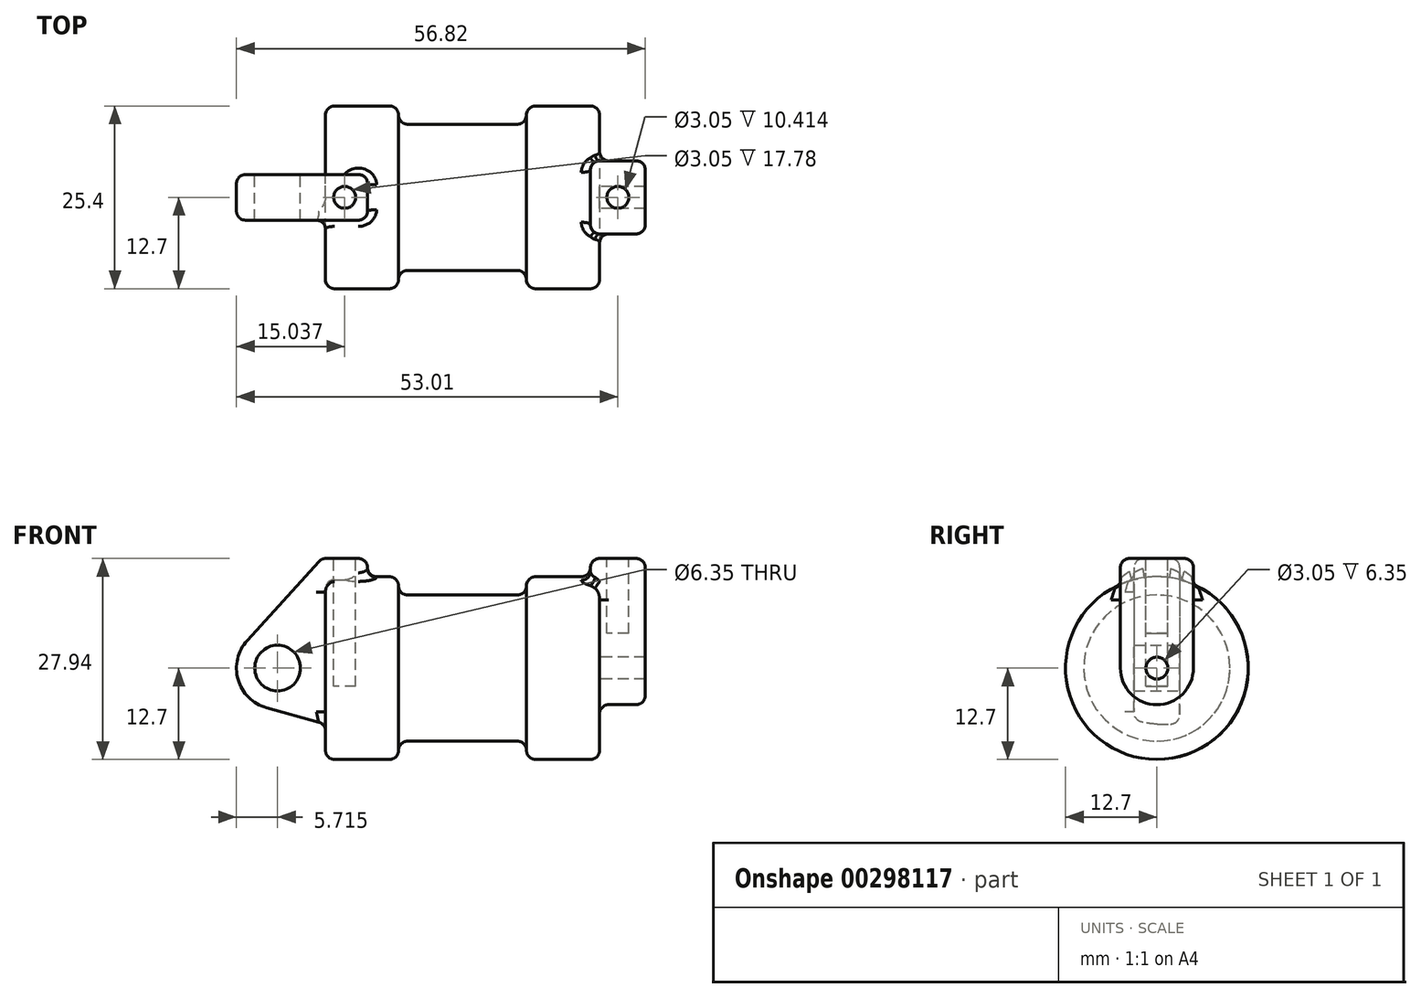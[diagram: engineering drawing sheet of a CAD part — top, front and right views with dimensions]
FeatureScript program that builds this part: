
annotation { "Feature Type Name" : "Feature", "Feature Type Description" : "" }
export const myFeature = defineFeature(function(context is Context, id is Id, definition is map)
    precondition{}
    {
        {
            var Q0;
            Q0=qCreatedBy(makeId("Front.planeOp"),FACE);
            var sketch = newSketch(context, id + "F0", { "sketchPlane" : qUnion([Q0])});
            skLineSegment(sketch, "E0", {"start": v(0, 0) * mm, "end": v(0, 12.7) * mm});
            skLineSegment(sketch, "E1", {"start": v(0, 12.7) * mm, "end": v(10.16, 12.7) * mm});
            skLineSegment(sketch, "E2", {"start": v(10.16, 12.7) * mm, "end": v(10.16, 10.16) * mm});
            skLineSegment(sketch, "E3", {"start": v(10.16, 10.16) * mm, "end": v(27.94, 10.16) * mm});
            skLineSegment(sketch, "E4", {"start": v(27.94, 10.16) * mm, "end": v(27.94, 12.7) * mm});
            skLineSegment(sketch, "E5", {"start": v(27.94, 12.7) * mm, "end": v(38.1, 12.7) * mm});
            skLineSegment(sketch, "E6", {"start": v(38.1, 12.7) * mm, "end": v(38.1, 0) * mm});
            skLineSegment(sketch, "E7", {"start": v(38.1, 0) * mm, "end": v(0, 0) * mm});
            skLineSegment(sketch, "E8", {"start": v(5.84, 15.24) * mm, "end": v(-0.5, 15.24) * mm});
            skLineSegment(sketch, "E9", {"start": v(-0.5, 15.24) * mm, "end": v(-10.88, 3.85) * mm});
            skLineSegment(sketch, "E10", {"start": v(0, 0) * mm, "end": v(-6.65, 0) * mm});
            skCircle(sketch, "E11", {"center": v(-6.65, 0) * mm, "radius": 5.72 * mm});
            skCircle(sketch, "E12", {"center": v(-6.65, 0) * mm, "radius": 3.18 * mm});
            skLineSegment(sketch, "E13", {"start": v(5.84, 15.24) * mm, "end": v(5.84, -9.4) * mm});
            skLineSegment(sketch, "E14", {"start": v(5.84, -9.4) * mm, "end": v(-8.18, -5.5) * mm});
            skSolve(sketch);
        }
        {
            var Q0;
            {var subQ0=sQuery(id+"F0.wireOp",EDGE,"E2");Q0=makeQuery(id+"F0.imprint","IMPRINT",FACE,{"disambiguationData":[TD([[makeQuery(id+"F0.imprint","IMPRINT",EDGE,{"derivedFrom":subQ0}),-1.0]])]});}
            var Q1;
            {var subQ0=sQuery(id+"F0.wireOp",EDGE,"E0");Q1=makeQuery(id+"F0.imprint","IMPRINT",FACE,{"disambiguationData":[TD([[makeQuery(id+"F0.imprint","IMPRINT",EDGE,{"derivedFrom":subQ0}),-1.0]])]});}
            var Q2;
            Q2=sQuery(id+"F0.wireOp",EDGE,"E7");
            revolve(context, id + "F1", {"entities" : qUnion([Q0, Q1]), "axis" : qUnion([Q2]), "revolveType" : RevolveType.FULL});
        }
        {
            var Q0;
            {var subQ1=sQuery(id+"F0.wireOp",EDGE,"E0");Q0=makeQuery(id+"F0.imprint","IMPRINT",FACE,{"disambiguationData":[TD([[makeQuery(id+"F0.imprint","IMPRINT",EDGE,{"derivedFrom":subQ1}),1.0]])]});}
            var Q1;
            Q1=makeQuery(id+"F0.imprint","IMPRINT",FACE,{"disambiguationData":[TD([[makeQuery(id+"F0.imprint","IMPRINT",EDGE,{"derivedFrom":sQuery(id+"F0.wireOp",EDGE,"E12")}),-1.0]])]});
            var Q2;
            {var subQ0=sQuery(id+"F0.wireOp",EDGE,"E14");Q2=makeQuery(id+"F0.imprint","IMPRINT",FACE,{"disambiguationData":[TD([[makeQuery(id+"F0.imprint","IMPRINT",EDGE,{"derivedFrom":subQ0}),-1.0]])]});}
            var Q3;
            {var subQ0=sQuery(id+"F0.wireOp",EDGE,"E0");Q3=makeQuery(id+"F0.imprint","IMPRINT",FACE,{"disambiguationData":[TD([[makeQuery(id+"F0.imprint","IMPRINT",EDGE,{"derivedFrom":subQ0}),-1.0]])]});}
            extrude(context, id + "F2", {"entities" : qUnion([Q0, Q1, Q2, Q3]), "operationType" : NewBodyOperationType.ADD, "endBound" : BoundingType.SYMMETRIC, "depth" : 6.35 * mm});
        }
        {
            var Q0;
            Q0=makeQuery(id+"F1.opRevolve","SWEPT_FACE",FACE,{"disambiguationData":[OSD([sQuery(id+"F0.wireOp",EDGE,"E6")])]});
            var sketch = newSketch(context, id + "F3", { "sketchPlane" : qUnion([Q0])});
            skCircle(sketch, "E15", {"center": v(0, 0) * mm, "radius": 5.08 * mm});
            skCircle(sketch, "E16", {"center": v(0, 0) * mm, "radius": 1.52 * mm});
            skLineSegment(sketch, "E17", {"start": v(-5.08, 0) * mm, "end": v(-5.08, 15.24) * mm});
            skLineSegment(sketch, "E18", {"start": v(5.08, 0) * mm, "end": v(5.08, 15.24) * mm});
            skLineSegment(sketch, "E19", {"start": v(5.08, 15.24) * mm, "end": v(-5.08, 15.24) * mm});
            skSolve(sketch);
        }
        {
            var Q0;
            {var subQ0=sQuery(id+"F3.wireOp",EDGE,"E19");Q0=makeQuery(id+"F3.imprint","IMPRINT",FACE,{"disambiguationData":[TD([[makeQuery(id+"F3.imprint","IMPRINT",EDGE,{"derivedFrom":subQ0}),1.0]])]});}
            var Q1;
            {var subQ0=sQuery(id+"F3.wireOp",EDGE,"E17");var subQ1=sQuery(id+"F3.wireOp",EDGE,"E15");var subQ2=makeQuery(id+"F3.imprint","INTERSECT",VERTEX,{"derivedFrom":[subQ1,subQ0]});Q1=makeQuery(id+"F3.imprint","IMPRINT",FACE,{"disambiguationData":[TD([[makeQuery(id+"F3.imprint","IMPRINT",EDGE,{"disambiguationData":[TD([[subQ2,1.0]])],"derivedFrom":subQ1}),-1.0]])]});}
            var Q2;
            Q2=makeQuery(id+"F3.imprint","IMPRINT",FACE,{"disambiguationData":[TD([[makeQuery(id+"F3.imprint","IMPRINT",EDGE,{"derivedFrom":sQuery(id+"F3.wireOp",EDGE,"E16")}),-1.0]])]});
            extrude(context, id + "F4", {"entities" : qUnion([Q0, Q1, Q2]), "operationType" : NewBodyOperationType.ADD, "depth" : 6.35 * mm, "hasSecondDirection" : true, "secondDirectionOppositeDirection" : true, "secondDirectionDepth" : 1.27 * mm});
        }
        {
            var Q0;
            Q0=makeQuery(id+"F4.opExtrude","SWEPT_FACE",FACE,{"disambiguationData":[OSD([sQuery(id+"F3.wireOp",EDGE,"E19")])]});
            var sketch = newSketch(context, id + "F5", { "sketchPlane" : qUnion([Q0])});
            skLineSegment(sketch, "E20", {"start": v(40.64, 5.08) * mm, "end": v(40.64, -5.08) * mm, "construction": true});
            skLineSegment(sketch, "E21", {"start": v(44.45, 0) * mm, "end": v(36.83, 0) * mm, "construction": true});
            skCircle(sketch, "E22", {"center": v(40.64, 0) * mm, "radius": 1.52 * mm});
            skSolve(sketch);
        }
        {
            var Q0;
            Q0=makeQuery(id+"F5.imprint","IMPRINT",FACE,{"disambiguationData":[TD([[makeQuery(id+"F5.imprint","IMPRINT",EDGE,{"derivedFrom":sQuery(id+"F5.wireOp",EDGE,"E22")}),1.0]])]});
            var Q1;
            Q1=sQuery(id+"F5.wireOp",EDGE,"E22");
            extrude(context, id + "F6", {"entities" : qUnion([Q0]), "operationType" : NewBodyOperationType.REMOVE, "surfaceEntities" : qUnion([Q1]), "oppositeDirection" : true, "depth" : 10.4 * mm});
        }
        {
            var Q0;
            Q0=makeQuery(id+"F2.opExtrude","SWEPT_FACE",FACE,{"disambiguationData":[OSD([sQuery(id+"F0.wireOp",EDGE,"E8")])]});
            var sketch = newSketch(context, id + "F7", { "sketchPlane" : qUnion([Q0])});
            skLineSegment(sketch, "E23", {"start": v(2.67, 3.18) * mm, "end": v(2.67, -3.18) * mm, "construction": true});
            skLineSegment(sketch, "E24", {"start": v(-0.5, 0) * mm, "end": v(5.84, 0) * mm, "construction": true});
            skCircle(sketch, "E25", {"center": v(2.67, 0) * mm, "radius": 1.52 * mm});
            skSolve(sketch);
        }
        {
            var Q0;
            Q0=makeQuery(id+"F7.imprint","IMPRINT",FACE,{"disambiguationData":[TD([[makeQuery(id+"F7.imprint","IMPRINT",EDGE,{"derivedFrom":sQuery(id+"F7.wireOp",EDGE,"E25")}),1.0]])]});
            var Q1;
            Q1=sQuery(id+"F7.wireOp",EDGE,"E25");
            extrude(context, id + "F8", {"entities" : qUnion([Q0]), "operationType" : NewBodyOperationType.REMOVE, "surfaceEntities" : qUnion([Q1]), "oppositeDirection" : true, "depth" : 17.78 * mm});
        }
        {
            var Q0;
            Q0=makeQuery(id+"F1.opRevolve","SWEPT_EDGE",EDGE,{"disambiguationData":[OSD([sQuery(id+"F0.wireOp",EDGE,"E2"),sQuery(id+"F0.wireOp",EDGE,"E3")])]});
            var Q1;
            Q1=makeQuery(id+"F1.opRevolve","SWEPT_EDGE",EDGE,{"disambiguationData":[OSD([sQuery(id+"F0.wireOp",EDGE,"E1"),sQuery(id+"F0.wireOp",EDGE,"E2")])]});
            var Q2;
            Q2=makeQuery(id+"F1.opRevolve","SWEPT_EDGE",EDGE,{"disambiguationData":[OSD([sQuery(id+"F0.wireOp",EDGE,"E0"),sQuery(id+"F0.wireOp",EDGE,"E1")])]});
            var Q3;
            Q3=makeQuery(id+"F1.opRevolve","SWEPT_EDGE",EDGE,{"disambiguationData":[OSD([sQuery(id+"F0.wireOp",EDGE,"E4"),sQuery(id+"F0.wireOp",EDGE,"E5")])]});
            var Q4;
            Q4=makeQuery(id+"F1.opRevolve","SWEPT_EDGE",EDGE,{"disambiguationData":[OSD([sQuery(id+"F0.wireOp",EDGE,"E5"),sQuery(id+"F0.wireOp",EDGE,"E6")])]});
            var Q5;
            Q5=makeQuery(id+"F1.opRevolve","SWEPT_EDGE",EDGE,{"disambiguationData":[OSD([sQuery(id+"F0.wireOp",EDGE,"E3"),sQuery(id+"F0.wireOp",EDGE,"E4")])]});
            fillet(context, id + "F9", {"entities" : qUnion([Q0, Q1, Q2, Q3, Q4, Q5]), "radius" : 1.27 * mm, "tangentPropagation" : true, "allowEdgeOverflow" : false});
        }
        {
            var Q0;
            Q0=makeQuery(id+"F2.opExtrude","CAP_EDGE",EDGE,{"disambiguationData":[OSD([sQuery(id+"F0.wireOp",EDGE,"E9")])],"isStart":false});
            var Q1;
            Q1=makeQuery(id+"F2.opExtrude","CAP_EDGE",EDGE,{"disambiguationData":[OSD([sQuery(id+"F0.wireOp",EDGE,"E9")])],"isStart":true});
            var Q2;
            Q2=makeQuery(id+"F2.boolean.opBoolean","INTERSECT",EDGE,{"derivedFrom":[makeQuery(id+"F1.opRevolve","SWEPT_FACE",FACE,{"disambiguationData":[OSD([sQuery(id+"F0.wireOp",EDGE,"E0")])]}),makeQuery(id+"F2.opExtrude","CAP_FACE",FACE,{"disambiguationData":[OSD([sQuery(id+"F0.wireOp",EDGE,"E8"),sQuery(id+"F0.wireOp",EDGE,"E9"),sQuery(id+"F0.wireOp",EDGE,"E11"),sQuery(id+"F0.wireOp",EDGE,"E12"),sQuery(id+"F0.wireOp",EDGE,"E13"),sQuery(id+"F0.wireOp",EDGE,"E14")])],"isStart":false})]});
            var Q3;
            Q3=makeQuery(id+"F2.opExtrude","CAP_EDGE",EDGE,{"disambiguationData":[OSD([sQuery(id+"F0.wireOp",EDGE,"E8")])],"isStart":false});
            var Q4;
            Q4=makeQuery(id+"F2.opExtrude","SWEPT_EDGE",EDGE,{"disambiguationData":[OSD([sQuery(id+"F0.wireOp",EDGE,"E8"),sQuery(id+"F0.wireOp",EDGE,"E9")])]});
            var Q5;
            Q5=makeQuery(id+"F2.opExtrude","CAP_EDGE",EDGE,{"disambiguationData":[OSD([sQuery(id+"F0.wireOp",EDGE,"E8")])],"isStart":true});
            var Q6;
            Q6=makeQuery(id+"F2.opExtrude","SWEPT_EDGE",EDGE,{"disambiguationData":[OSD([sQuery(id+"F0.wireOp",EDGE,"E8"),sQuery(id+"F0.wireOp",EDGE,"E13")])]});
            var Q7;
            Q7=makeQuery(id+"F2.boolean.opBoolean","INTERSECT",EDGE,{"derivedFrom":[makeQuery(id+"F1.opRevolve","SWEPT_FACE",FACE,{"disambiguationData":[OSD([sQuery(id+"F0.wireOp",EDGE,"E1")])]}),makeQuery(id+"F2.opExtrude","SWEPT_FACE",FACE,{"disambiguationData":[OSD([sQuery(id+"F0.wireOp",EDGE,"E13")])]})]});
            var Q8;
            Q8=makeQuery(id+"F2.opExtrude","CAP_EDGE",EDGE,{"disambiguationData":[OSD([sQuery(id+"F0.wireOp",EDGE,"E13")])],"isStart":false});
            var Q9;
            Q9=makeQuery(id+"F2.opExtrude","CAP_EDGE",EDGE,{"disambiguationData":[OSD([sQuery(id+"F0.wireOp",EDGE,"E13")])],"isStart":true});
            fillet(context, id + "F10", {"entities" : qUnion([Q0, Q1, Q2, Q3, Q4, Q5, Q6, Q7, Q8, Q9]), "radius" : 1.27 * mm, "tangentPropagation" : true, "allowEdgeOverflow" : false});
        }
        {
            var Q0;
            Q0=makeQuery(id+"F4.boolean.opBoolean","INTERSECT",EDGE,{"derivedFrom":[makeQuery(id+"F1.opRevolve","SWEPT_FACE",FACE,{"disambiguationData":[OSD([sQuery(id+"F0.wireOp",EDGE,"E6")])]}),makeQuery(id+"F4.opExtrude","SWEPT_FACE",FACE,{"disambiguationData":[OSD([sQuery(id+"F3.wireOp",EDGE,"E17")])]})]});
            var Q1;
            Q1=makeQuery(id+"F4.opExtrude","SWEPT_EDGE",EDGE,{"disambiguationData":[OSD([sQuery(id+"F3.wireOp",EDGE,"E17"),sQuery(id+"F3.wireOp",EDGE,"E19")])]});
            var Q2;
            Q2=makeQuery(id+"F4.opExtrude","CAP_EDGE",EDGE,{"disambiguationData":[OSD([sQuery(id+"F3.wireOp",EDGE,"E19")])],"isStart":false});
            var Q3;
            Q3=makeQuery(id+"F4.opExtrude","SWEPT_EDGE",EDGE,{"disambiguationData":[OSD([sQuery(id+"F3.wireOp",EDGE,"E18"),sQuery(id+"F3.wireOp",EDGE,"E19")])]});
            var Q4;
            Q4=makeQuery(id+"F4.opExtrude","CAP_EDGE",EDGE,{"disambiguationData":[OSD([sQuery(id+"F3.wireOp",EDGE,"E19")])],"isStart":true});
            var Q5;
            Q5=makeQuery(id+"F4.opExtrude","CAP_EDGE",EDGE,{"disambiguationData":[OSD([sQuery(id+"F3.wireOp",EDGE,"E18")])],"isStart":false});
            var Q6;
            Q6=makeQuery(id+"F4.boolean.opBoolean","INTERSECT",EDGE,{"derivedFrom":[makeQuery(id+"F1.opRevolve","SWEPT_FACE",FACE,{"disambiguationData":[OSD([sQuery(id+"F0.wireOp",EDGE,"E5")])]}),makeQuery(id+"F4.opExtrude","CAP_FACE",FACE,{"disambiguationData":[OSD([sQuery(id+"F3.wireOp",EDGE,"E15"),sQuery(id+"F3.wireOp",EDGE,"E16"),sQuery(id+"F3.wireOp",EDGE,"E17"),sQuery(id+"F3.wireOp",EDGE,"E18"),sQuery(id+"F3.wireOp",EDGE,"E19")])],"isStart":true})]});
            var Q7;
            Q7=makeQuery(id+"F4.opExtrude","CAP_EDGE",EDGE,{"disambiguationData":[OSD([sQuery(id+"F3.wireOp",EDGE,"E17")])],"isStart":true});
            var Q8;
            Q8=makeQuery(id+"F4.opExtrude","CAP_EDGE",EDGE,{"disambiguationData":[OSD([sQuery(id+"F3.wireOp",EDGE,"E18")])],"isStart":true});
            fillet(context, id + "F11", {"entities" : qUnion([Q0, Q1, Q2, Q3, Q4, Q5, Q6, Q7, Q8]), "radius" : 1.27 * mm, "tangentPropagation" : true, "allowEdgeOverflow" : false});
        }
    });
